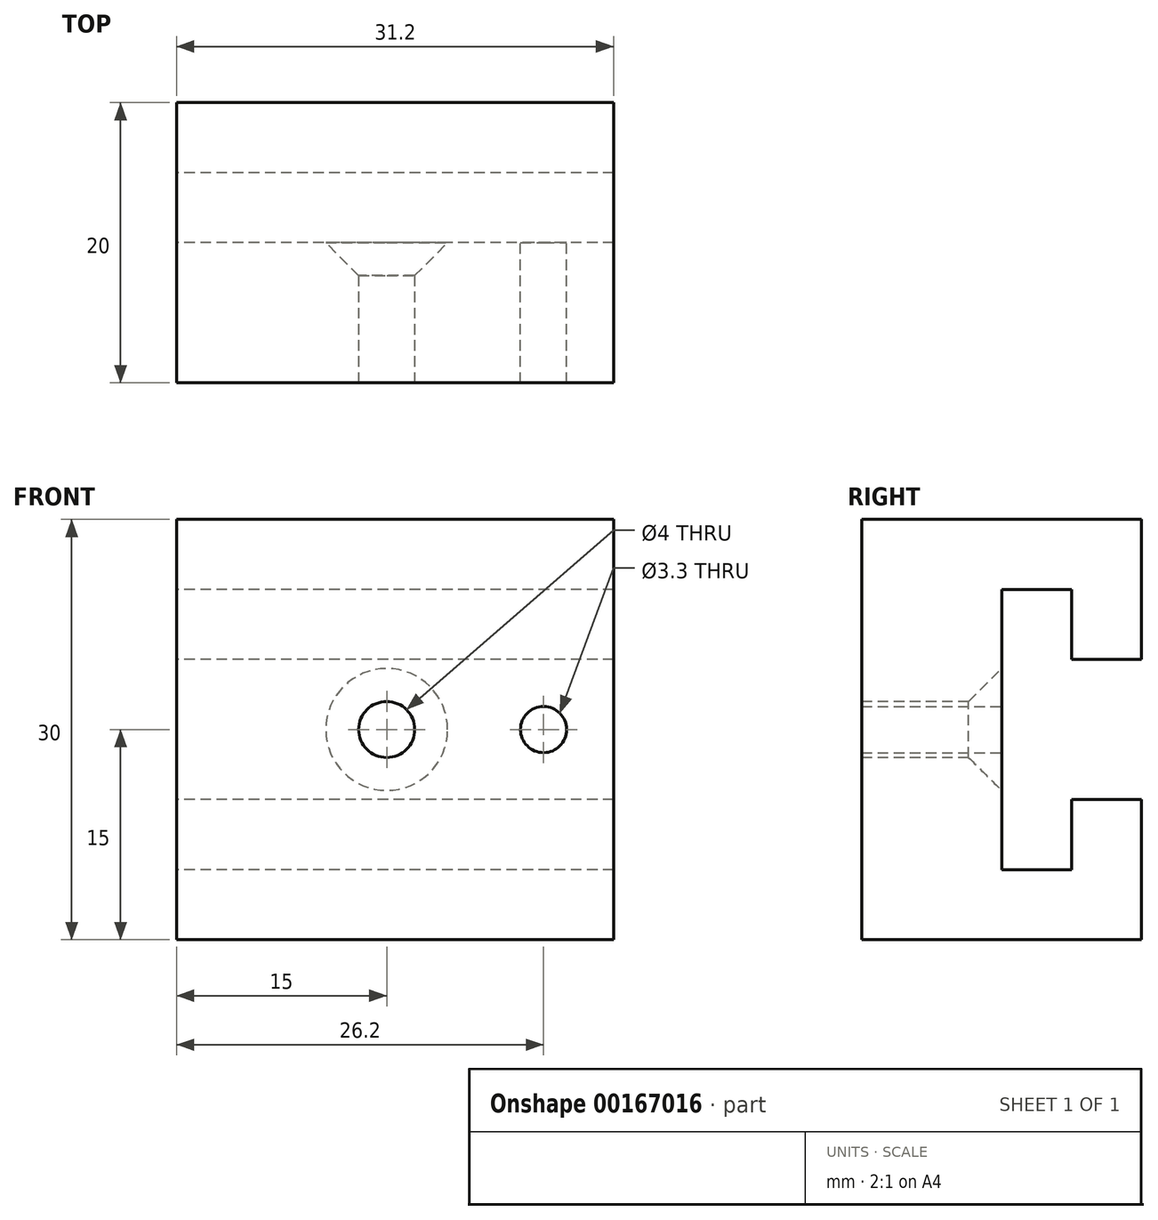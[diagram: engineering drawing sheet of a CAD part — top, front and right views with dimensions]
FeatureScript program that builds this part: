
annotation { "Feature Type Name" : "Feature", "Feature Type Description" : "" }
export const myFeature = defineFeature(function(context is Context, id is Id, definition is map)
    precondition{}
    {
        {
            var Q0;
            Q0=qCreatedBy(makeId("Right.planeOp"),FACE);
            var sketch = newSketch(context, id + "F0", { "sketchPlane" : qUnion([Q0])});
            skLineSegment(sketch, "E0", {"start": v(0, 0) * mm, "end": v(0, 30) * mm});
            skLineSegment(sketch, "E1", {"start": v(0, 30) * mm, "end": v(20, 30) * mm});
            skLineSegment(sketch, "E2", {"start": v(20, 30) * mm, "end": v(20, 25) * mm});
            skLineSegment(sketch, "E3", {"start": v(20, 25) * mm, "end": v(10, 25) * mm});
            skLineSegment(sketch, "E4", {"start": v(0, 15) * mm, "end": v(6.1, 15) * mm});
            skLineSegment(sketch, "E5", {"start": v(10, 25) * mm, "end": v(10, 15) * mm});
            skLineSegment(sketch, "E6.MirrorCS", {"start": v(10, 5) * mm, "end": v(10, 15) * mm});
            skLineSegment(sketch, "E7.MirrorCS", {"start": v(20, 5) * mm, "end": v(10, 5) * mm});
            skLineSegment(sketch, "E8.MirrorCS", {"start": v(20, 0) * mm, "end": v(20, 5) * mm});
            skLineSegment(sketch, "E9.MirrorCS", {"start": v(0, 0) * mm, "end": v(20, 0) * mm});
            skLineSegment(sketch, "E10", {"start": v(10, 15) * mm, "end": v(0, 15) * mm});
            skLineSegment(sketch, "E11", {"start": v(20, 25) * mm, "end": v(20, 20) * mm});
            skLineSegment(sketch, "E12", {"start": v(20, 20) * mm, "end": v(15, 20) * mm});
            skLineSegment(sketch, "E13", {"start": v(15, 20) * mm, "end": v(15, 25) * mm});
            skLineSegment(sketch, "E14.MirrorCS", {"start": v(20, 5) * mm, "end": v(20, 10) * mm});
            skLineSegment(sketch, "E15.MirrorCS", {"start": v(15, 10) * mm, "end": v(15, 5) * mm});
            skLineSegment(sketch, "E16.MirrorCS", {"start": v(20, 10) * mm, "end": v(15, 10) * mm});
            skSolve(sketch);
        }
        {
            var Q0;
            {var subQ3=sQuery(id+"F0.wireOp",EDGE,"E1");Q0=makeQuery(id+"F0.imprint","IMPRINT",FACE,{"disambiguationData":[TD([[makeQuery(id+"F0.imprint","IMPRINT",EDGE,{"derivedFrom":subQ3}),-1.0]])]});}
            var Q1;
            {var subQ0=sQuery(id+"F0.wireOp",EDGE,"E11");Q1=makeQuery(id+"F0.imprint","IMPRINT",FACE,{"disambiguationData":[TD([[makeQuery(id+"F0.imprint","IMPRINT",EDGE,{"derivedFrom":subQ0}),-1.0]])]});}
            var Q2;
            {var subQ0=sQuery(id+"F0.wireOp",EDGE,"E14.MirrorCS");Q2=makeQuery(id+"F0.imprint","IMPRINT",FACE,{"disambiguationData":[TD([[makeQuery(id+"F0.imprint","IMPRINT",EDGE,{"derivedFrom":subQ0}),1.0]])]});}
            var Q3;
            {var subQ1=sQuery(id+"F0.wireOp",EDGE,"E6.MirrorCS");Q3=makeQuery(id+"F0.imprint","IMPRINT",FACE,{"disambiguationData":[TD([[makeQuery(id+"F0.imprint","IMPRINT",EDGE,{"derivedFrom":subQ1}),1.0]])]});}
            extrude(context, id + "F1", {"entities" : qUnion([Q0, Q1, Q2, Q3]), "depth" : 200 * mm});
        }
        {
            var Q0;
            Q0=makeQuery(id+"F1.opExtrude","CAP_FACE",FACE,{"disambiguationData":[OSD([sQuery(id+"F0.wireOp",EDGE,"E0"),sQuery(id+"F0.wireOp",EDGE,"E1"),sQuery(id+"F0.wireOp",EDGE,"E2"),sQuery(id+"F0.wireOp",EDGE,"E3"),sQuery(id+"F0.wireOp",EDGE,"E5"),sQuery(id+"F0.wireOp",EDGE,"E6.MirrorCS"),sQuery(id+"F0.wireOp",EDGE,"E7.MirrorCS"),sQuery(id+"F0.wireOp",EDGE,"E8.MirrorCS"),sQuery(id+"F0.wireOp",EDGE,"E9.MirrorCS"),sQuery(id+"F0.wireOp",EDGE,"E11"),sQuery(id+"F0.wireOp",EDGE,"E12"),sQuery(id+"F0.wireOp",EDGE,"E13"),sQuery(id+"F0.wireOp",EDGE,"E14.MirrorCS"),sQuery(id+"F0.wireOp",EDGE,"E15.MirrorCS"),sQuery(id+"F0.wireOp",EDGE,"E16.MirrorCS")])],"isStart":false});
            var sketch = newSketch(context, id + "F2", { "sketchPlane" : qUnion([Q0])});
            skLineSegment(sketch, "E17", {"start": v(0, 30) * mm, "end": v(20, 30) * mm});
            skLineSegment(sketch, "E18", {"start": v(20, 30) * mm, "end": v(20, 0) * mm});
            skLineSegment(sketch, "E19", {"start": v(20, 0) * mm, "end": v(0, 0) * mm});
            skLineSegment(sketch, "E20", {"start": v(0, 0) * mm, "end": v(0, 30) * mm});
            skSolve(sketch);
        }
        {
            var Q0;
            {var subQ4=sQuery(id+"F2.wireOp",EDGE,"E17");Q0=makeQuery(id+"F2.imprint","IMPRINT",FACE,{"disambiguationData":[TD([[makeQuery(id+"F2.imprint","IMPRINT",EDGE,{"derivedFrom":subQ4}),-1.0]])]});}
            var Q1;
            Q1=makeQuery(id+"F2.imprint","IMPRINT",FACE,{"disambiguationData":[TD([[makeQuery(id+"F2.imprint","IMPRINT",EDGE,{"derivedFrom":makeQuery(id+"F1.opExtrude","CAP_EDGE",EDGE,{"disambiguationData":[OSD([sQuery(id+"F0.wireOp",EDGE,"E3")])],"isStart":false})}),1.0]])]});
            extrude(context, id + "F3", {"entities" : qUnion([Q0, Q1]), "operationType" : NewBodyOperationType.ADD, "depth" : 1.2 * mm});
        }
        {
            var Q0;
            Q0=makeQuery(id+"F1.opExtrude","SWEPT_FACE",FACE,{"disambiguationData":[OSD([sQuery(id+"F0.wireOp",EDGE,"E5"),sQuery(id+"F0.wireOp",EDGE,"E6.MirrorCS")])]});
            var sketch = newSketch(context, id + "F4", { "sketchPlane" : qUnion([Q0])});
            skLineSegment(sketch, "E21", {"start": v(0, 15) * mm, "end": v(-200, 15) * mm});
            skLineSegment(sketch, "E22", {"start": v(-200, 15) * mm, "end": v(-100, 15) * mm});
            skLineSegment(sketch, "E23", {"start": v(-100, 15) * mm, "end": v(-100, 17.07) * mm});
            skLineSegment(sketch, "E24", {"start": v(-200, 15) * mm, "end": v(-185, 15) * mm});
            skLineSegment(sketch, "E25", {"start": v(0, 15) * mm, "end": v(-15, 15) * mm});
            skSolve(sketch);
        }
        {
            var Q0;
            Q0=sQuery(id+"F4.wireOp",VERTEX,"E25.end");
            var Q1;
            Q1=sQuery(id+"F4.wireOp",VERTEX,"E24.end");
            var Q2;
            Q2=sQuery(id+"F4.wireOp",VERTEX,"E23.start");
            var Q3;
            Q3=makeQuery(id+"F1.opExtrude","SWEPT_BODY",BODY,{"disambiguationData":[OSD([sQuery(id+"F0.wireOp",EDGE,"E0"),sQuery(id+"F0.wireOp",EDGE,"E1"),sQuery(id+"F0.wireOp",EDGE,"E2"),sQuery(id+"F0.wireOp",EDGE,"E3"),sQuery(id+"F0.wireOp",EDGE,"E5"),sQuery(id+"F0.wireOp",EDGE,"E6.MirrorCS"),sQuery(id+"F0.wireOp",EDGE,"E7.MirrorCS"),sQuery(id+"F0.wireOp",EDGE,"E8.MirrorCS"),sQuery(id+"F0.wireOp",EDGE,"E9.MirrorCS"),sQuery(id+"F0.wireOp",EDGE,"E11"),sQuery(id+"F0.wireOp",EDGE,"E12"),sQuery(id+"F0.wireOp",EDGE,"E13"),sQuery(id+"F0.wireOp",EDGE,"E14.MirrorCS"),sQuery(id+"F0.wireOp",EDGE,"E15.MirrorCS"),sQuery(id+"F0.wireOp",EDGE,"E16.MirrorCS")])]});
            hole(context, id + "F5", {"style" : HoleStyle.C_SINK, "endStyle" : HoleEndStyle.THROUGH, "holeDiameter" : 4 * mm, "cSinkDiameter" : 8.7 * mm, "cSinkAngle" : 90 * degree, "locations" : qUnion([Q0, Q1, Q2]), "scope" : qUnion([Q3]), "isTappedThrough" : true, "startStyle" : HoleStartStyle.PART});
        }
        {
            var Q0;
            Q0=makeQuery(id+"F3.opExtrude","CAP_FACE",FACE,{"disambiguationData":[OSD([sQuery(id+"F2.wireOp",EDGE,"E17"),sQuery(id+"F2.wireOp",EDGE,"E18"),sQuery(id+"F2.wireOp",EDGE,"E19"),sQuery(id+"F2.wireOp",EDGE,"E20")])],"isStart":false});
            extrude(context, id + "F6", {"entities" : qUnion([Q0]), "operationType" : NewBodyOperationType.REMOVE, "oppositeDirection" : true, "depth" : 170 * mm});
        }
        {
            var Q0;
            Q0=makeQuery(id+"F1.opExtrude","SWEPT_FACE",FACE,{"disambiguationData":[OSD([sQuery(id+"F0.wireOp",EDGE,"E5"),sQuery(id+"F0.wireOp",EDGE,"E6.MirrorCS")])]});
            var sketch = newSketch(context, id + "F7", { "sketchPlane" : qUnion([Q0])});
            skLineSegment(sketch, "E26", {"start": v(-31.2, 15) * mm, "end": v(-26.2, 15) * mm});
            skCircle(sketch, "E27", {"center": v(-26.2, 15) * mm, "radius": 1.65 * mm});
            skSolve(sketch);
        }
        {
            var Q0;
            Q0 = qSketchRegion(id + "F7", true);
            var Q1;
            Q1=makeQuery(id+"F7.imprint","IMPRINT",FACE,{"disambiguationData":[TD([[makeQuery(id+"F7.imprint","IMPRINT",EDGE,{"derivedFrom":sQuery(id+"F7.wireOp",EDGE,"E27")}),1.0]])]});
            extrude(context, id + "F8", {"entities" : qUnion([Q0, Q1]), "operationType" : NewBodyOperationType.REMOVE, "oppositeDirection" : true, "depth" : 25 * mm});
        }
    });
